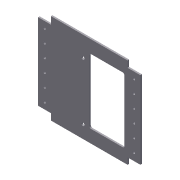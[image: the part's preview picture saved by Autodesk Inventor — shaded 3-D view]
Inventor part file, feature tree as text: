
AUTODESK INVENTOR PART (.ipt)
format: ipt  version: 2012 (Build 160160000, 160)  size: 151,552 bytes
history: native  units: in
note: dims shown in document units (in); Inventor stores cm internally (conversion verified against a paired STEP export)
features: extrude x4, sketch x4
ambient origin geometry x8: Origin, YZ Plane, XZ Plane, XY Plane, X Axis, Y Axis, Z Axis, Center Point
feature tree (8):
  extrude  "Extrusion3"  Depth=8.0in
  extrude  "Extrusion4"  Depth=1.0in
  extrude  "Extrusion5"  Depth=1.0in
  extrude  "Extrusion6"  Depth=0.5in
  sketch  "Sketch1"  dims[d0=6.0in d1=8.0in]
  sketch  "Sketch2"  dims[d18=1.0in d19=1.0in]
  sketch  "Sketch3"  dims[d20=0.5in d21=1.0in]
  sketch  "Sketch4"  dims[d22=1.0in d23=0.5in d24=0.125in d25=0.0in d26=0.5in d27=1.0in d28=0.1875in d29=0.5in d30=1.0in d31=0.1875in d32=0.125in d33=0.0in d34=3.5in d35=3.5in d36=4.5in d37=0.5in d38=0.25in d39=0.25in d40=0.125in d41=0.0in d42=0.5in d43=1.25in d44=0.5in d45=0.5in d46=0.125in d47=0.125in d48=0.0in]
